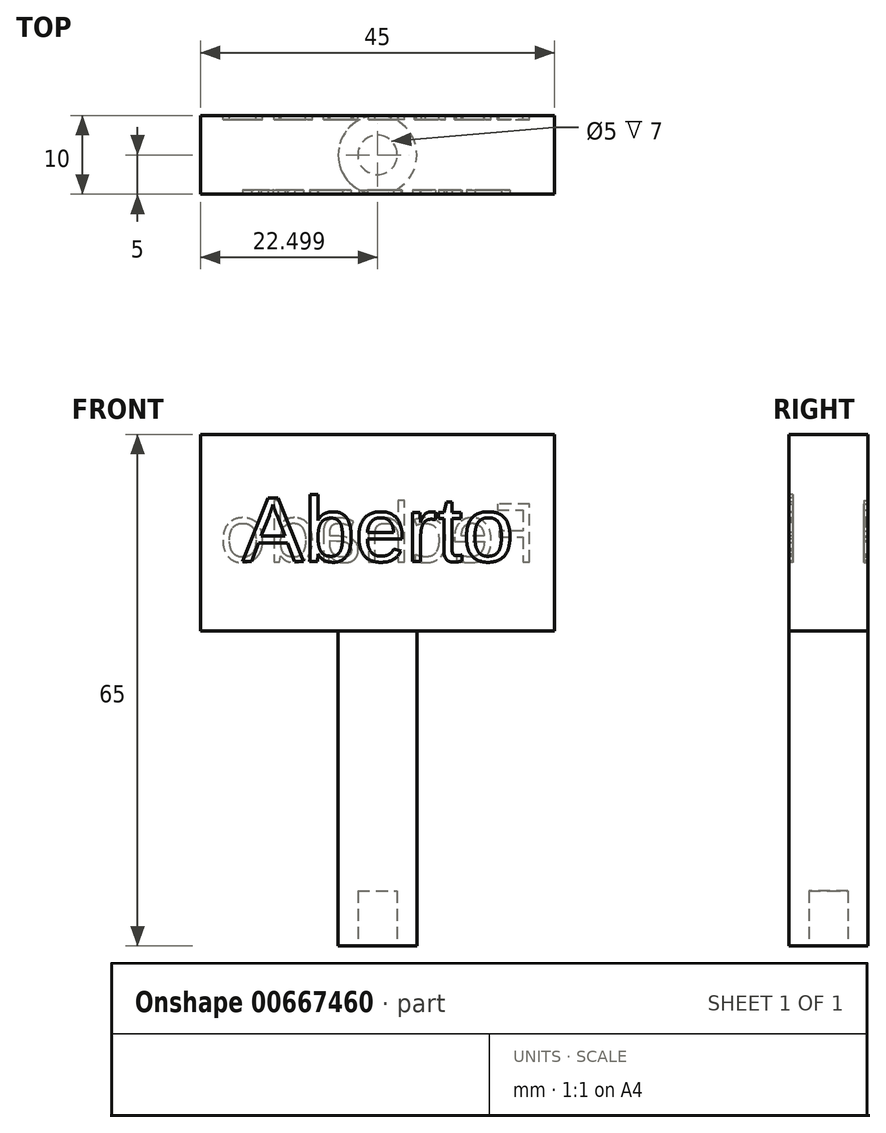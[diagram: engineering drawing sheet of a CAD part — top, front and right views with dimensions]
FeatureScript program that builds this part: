
annotation { "Feature Type Name" : "Feature", "Feature Type Description" : "" }
export const myFeature = defineFeature(function(context is Context, id is Id, definition is map)
    precondition{}
    {
        {
            var Q0;
            Q0=qCreatedBy(makeId("Front.planeOp"),FACE);
            var sketch = newSketch(context, id + "F0", { "sketchPlane" : qUnion([Q0])});
            skLineSegment(sketch, "E0.bottom", {"start": v(-46.37, -9.34) * mm, "end": v(-1.37, -9.34) * mm});
            skLineSegment(sketch, "E0.top", {"start": v(-46.37, -34.34) * mm, "end": v(-1.37, -34.34) * mm});
            skLineSegment(sketch, "E0.left", {"start": v(-46.37, -9.34) * mm, "end": v(-46.37, -34.34) * mm});
            skLineSegment(sketch, "E0.right", {"start": v(-1.37, -9.34) * mm, "end": v(-1.37, -34.34) * mm});
            skSolve(sketch);
        }
        {
            var Q0;
            Q0=makeQuery(id+"F0.imprint","IMPRINT",FACE,{"disambiguationData":[TD([[makeQuery(id+"F0.imprint","IMPRINT",EDGE,{"derivedFrom":sQuery(id+"F0.wireOp",EDGE,"E0.bottom")}),-1.0]])]});
            extrude(context, id + "F1", {"entities" : qUnion([Q0]), "depth" : 10 * mm, "offsetDistance" : 25.4 * mm});
        }
        {
            var Q0;
            Q0=makeQuery(id+"F1.opExtrude","CAP_FACE",FACE,{"disambiguationData":[OSD([sQuery(id+"F0.wireOp",EDGE,"E0.bottom"),sQuery(id+"F0.wireOp",EDGE,"E0.top"),sQuery(id+"F0.wireOp",EDGE,"E0.left"),sQuery(id+"F0.wireOp",EDGE,"E0.right")])],"isStart":false});
            var sketch = newSketch(context, id + "F2", { "sketchPlane" : qUnion([Q0])});
            skText(sketch, "E1", { "text": "Aberto", "fontName": "Arimo-Regular.ttf"});
            const initialGuessF2  = {"E1": [-0.04106, -0.02548, 1, 0, 0.00843]};
            skSetInitialGuess(sketch, initialGuessF2);
            skSolve(sketch);
        }
        {
            var Q0;
            Q0 = qSketchRegion(id + "F2", true);
            extrude(context, id + "F3", {"entities" : qUnion([Q0]), "operationType" : NewBodyOperationType.REMOVE, "oppositeDirection" : true, "depth" : 0.5 * mm, "offsetDistance" : 25.4 * mm});
        }
        {
            var Q0;
            Q0=makeQuery(id+"F1.opExtrude","CAP_FACE",FACE,{"disambiguationData":[OSD([sQuery(id+"F0.wireOp",EDGE,"E0.bottom"),sQuery(id+"F0.wireOp",EDGE,"E0.top"),sQuery(id+"F0.wireOp",EDGE,"E0.left"),sQuery(id+"F0.wireOp",EDGE,"E0.right")])],"isStart":true});
            var sketch = newSketch(context, id + "F4", { "sketchPlane" : qUnion([Q0])});
            skText(sketch, "E2", { "text": "Fechado\n", "fontName": "OpenSans-Regular.ttf"});
            const initialGuessF4  = {"E2": [0.00355, -0.02554, 1, 0, 0.00741]};
            skSetInitialGuess(sketch, initialGuessF4);
            skSolve(sketch);
        }
        {
            var Q0;
            Q0 = qSketchRegion(id + "F4", true);
            extrude(context, id + "F5", {"entities" : qUnion([Q0]), "operationType" : NewBodyOperationType.REMOVE, "oppositeDirection" : true, "depth" : 0.5 * mm, "offsetDistance" : 25.4 * mm});
        }
        {
            var Q0;
            Q0=makeQuery(id+"F1.opExtrude","SWEPT_FACE",FACE,{"disambiguationData":[OSD([sQuery(id+"F0.wireOp",EDGE,"E0.top")])]});
            var sketch = newSketch(context, id + "F6", { "sketchPlane" : qUnion([Q0])});
            skCircle(sketch, "E3", {"center": v(-23.87, 5) * mm, "radius": 5 * mm});
            skSolve(sketch);
        }
        {
            var Q0;
            Q0 = qSketchRegion(id + "F6", true);
            extrude(context, id + "F7", {"entities" : qUnion([Q0]), "operationType" : NewBodyOperationType.ADD, "depth" : 40 * mm, "offsetDistance" : 25.4 * mm});
        }
        {
            var Q0;
            Q0=makeQuery(id+"F7.opExtrude","CAP_FACE",FACE,{"disambiguationData":[OSD([sQuery(id+"F6.wireOp",EDGE,"E3")])],"isStart":false});
            var sketch = newSketch(context, id + "F8", { "sketchPlane" : qUnion([Q0])});
            skCircle(sketch, "E4", {"center": v(-23.87, 5) * mm, "radius": 2.5 * mm});
            skSolve(sketch);
        }
        {
            var Q0;
            Q0=makeQuery(id+"F8.imprint","IMPRINT",FACE,{"disambiguationData":[TD([[makeQuery(id+"F8.imprint","IMPRINT",EDGE,{"derivedFrom":sQuery(id+"F8.wireOp",EDGE,"E4")}),1.0]])]});
            extrude(context, id + "F9", {"entities" : qUnion([Q0]), "operationType" : NewBodyOperationType.REMOVE, "oppositeDirection" : true, "depth" : 7 * mm, "offsetDistance" : 25.4 * mm});
        }
    });
